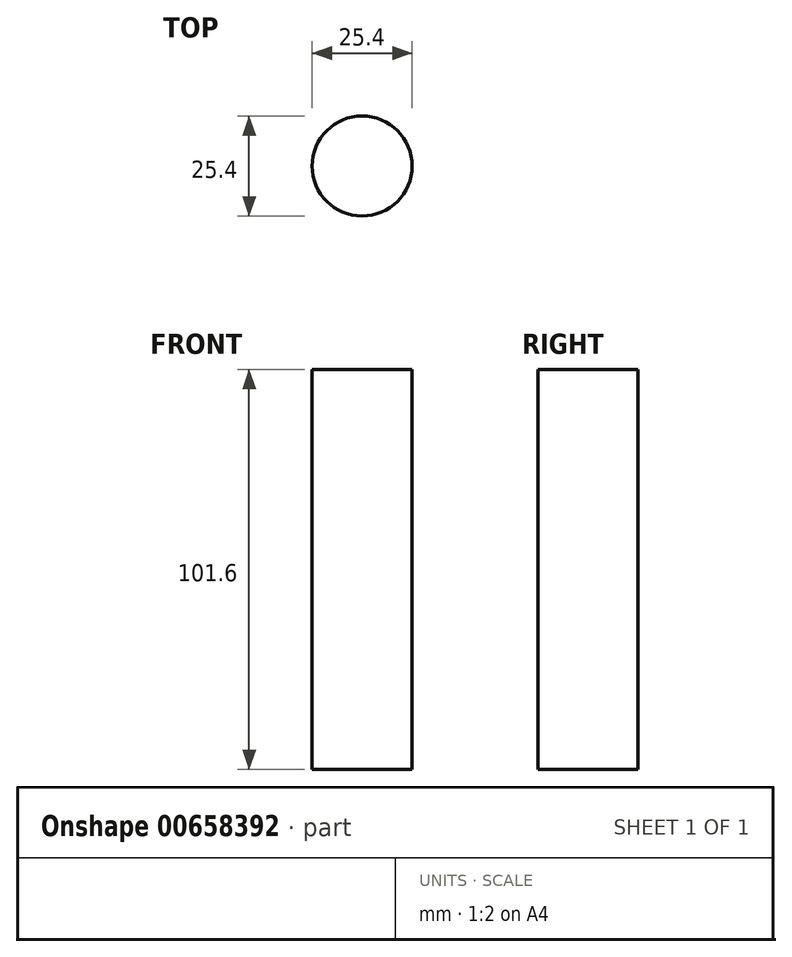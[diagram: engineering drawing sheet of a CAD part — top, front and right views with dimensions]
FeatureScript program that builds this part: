
annotation { "Feature Type Name" : "Feature", "Feature Type Description" : "" }
export const myFeature = defineFeature(function(context is Context, id is Id, definition is map)
    precondition{}
    {
        {
            var Q0;
            Q0=qCreatedBy(makeId("Top.planeOp"),FACE);
            var sketch = newSketch(context, id + "F0", { "sketchPlane" : qUnion([Q0])});
            skCircle(sketch, "E0", {"center": v(0, 0) * mm, "radius": 12.7 * mm});
            skSolve(sketch);
        }
        {
            var Q0;
            Q0=makeQuery(id+"F0.imprint","IMPRINT",FACE,{"disambiguationData":[TD([[makeQuery(id+"F0.imprint","IMPRINT",EDGE,{"derivedFrom":sQuery(id+"F0.wireOp",EDGE,"E0")}),1.0]])]});
            var Q1;
            Q1=sQuery(id+"F0.wireOp",EDGE,"E0");
            extrude(context, id + "F1", {"entities" : qUnion([Q0]), "surfaceEntities" : qUnion([Q1]), "depth" : 101.6 * mm, "offsetDistance" : 25.4 * mm});
        }
    });
